# Revit family: Wide Flange-Profile
name_source: partatom
category: Profiles
revit_build: Autodesk Revit Architecture 2012 (Build: 20110210_1515)
units: mm (PartAtom-declared; Revit-internal decimal feet)

## types (267) — shared parameters

## per-type parameters (varying)
| type | A | W | bf | d | k | tf | tw |
| W44X335 | 0.68 SF | 335 | 1' - 3 15/16" | 3' - 8 1/32" | 0' - 2 5/8" | 0' - 1 25/32" | 0' - 1 1/32" |
| W44X290 | 0.6 SF | 290 | 1' - 3 13/16" | 3' - 7 5/8" | 0' - 2 7/16" | 0' - 1 9/16" | 0' - 0 7/8" |
| W44X262 | 0.54 SF | 262 | 1' - 3 3/4" | 3' - 7 5/16" | 0' - 2 1/4" | 0' - 1 13/32" | 0' - 0 25/32" |
| W44X230 | 0.47 SF | 230 | 1' - 3 3/4" | 3' - 6 29/32" | 0' - 2 1/16" | 0' - 1 7/32" | 0' - 0 23/32" |
| W40X593 | 1.21 SF | 593 | 1' - 4 11/16" | 3' - 7" | 0' - 4 1/2" | 0' - 3 7/32" | 0' - 1 25/32" |
| W40X503 | 1.03 SF | 503 | 1' - 4 13/32" | 3' - 6 1/16" | 0' - 4" | 0' - 2 3/4" | 0' - 1 17/32" |
| W40X431 | 0.88 SF | 431 | 1' - 4 7/32" | 3' - 5 1/4" | 0' - 3 5/8" | 0' - 2 3/8" | 0' - 1 11/32" |
| W40X397 | 0.81 SF | 397 | 1' - 4 1/8" | 3' - 4 15/16" | 0' - 3 1/2" | 0' - 2 3/16" | 0' - 1 7/32" |
| W40X372 | 0.76 SF | 372 | 1' - 4 1/16" | 3' - 4 5/8" | 0' - 3 5/16" | 0' - 2 1/32" | 0' - 1 5/32" |
| W40X362 | 0.74 SF | 362 | 1' - 4 1/32" | 3' - 4 9/16" | 0' - 3 1/4" | 0' - 2" | 0' - 1 1/8" |
| W40X324 | 0.66 SF | 324 | 1' - 3 29/32" | 3' - 4 5/32" | 0' - 3 1/16" | 0' - 1 13/16" | 0' - 1" |
| W40X297 | 0.61 SF | 297 | 1' - 3 13/16" | 3' - 3 27/32" | 0' - 2 15/16" | 0' - 1 21/32" | 0' - 0 15/16" |
| W40X277 | 0.57 SF | 277 | 1' - 3 27/32" | 3' - 3 11/16" | 0' - 2 7/8" | 0' - 1 9/16" | 0' - 0 27/32" |
| W40X249 | 0.51 SF | 249 | 1' - 3 3/4" | 3' - 3 3/8" | 0' - 2 11/16" | 0' - 1 13/32" | 0' - 0 3/4" |
| W40X215 | 0.44 SF | 215 | 1' - 3 3/4" | 3' - 2 31/32" | 0' - 2 1/2" | 0' - 1 7/32" | 0' - 0 21/32" |
| W40X199 | 0.41 SF | 199 | 1' - 3 3/4" | 3' - 2 21/32" | 0' - 2 5/16" | 0' - 1 1/16" | 0' - 0 21/32" |
| W40X392 | 0.8 SF | 392 | 1' - 0 3/8" | 3' - 5 9/16" | 0' - 3 13/16" | 0' - 2 17/32" | 0' - 1 13/32" |
| W40X331 | 0.68 SF | 331 | 1' - 0 5/32" | 3' - 4 5/32" | 0' - 3 3/8" | 0' - 2 1/8" | 0' - 1 7/32" |
| W40X327 | 0.67 SF | 327 | 1' - 0 1/8" | 3' - 4 13/16" | 0' - 3 3/8" | 0' - 2 1/8" | 0' - 1 3/16" |
| W40X278 | 0.57 SF | 278 | 1' - 0" | 3' - 4 5/32" | 0' - 3 1/16" | 0' - 1 13/16" | 0' - 1 1/32" |
| W40X264 | 0.54 SF | 264 | 0' - 11 31/32" | 3' - 4" | 0' - 3" | 0' - 1 23/32" | 0' - 0 31/32" |
| W40X235 | 0.48 SF | 235 | 0' - 11 15/16" | 3' - 3 11/16" | 0' - 2 7/8" | 0' - 1 9/16" | 0' - 0 27/32" |
| W40X211 | 0.43 SF | 211 | 0' - 11 7/8" | 3' - 3 3/8" | 0' - 2 11/16" | 0' - 1 13/32" | 0' - 0 3/4" |
| W40X183 | 0.37 SF | 183 | 0' - 11 13/16" | 3' - 2 31/32" | 0' - 2 1/2" | 0' - 1 3/16" | 0' - 0 21/32" |
| W40X167 | 0.34 SF | 167 | 0' - 11 13/16" | 3' - 2 19/32" | 0' - 2 5/16" | 0' - 1 1/32" | 0' - 0 21/32" |
| W40X149 | 0.3 SF | 149 | 0' - 11 13/16" | 3' - 2 3/16" | 0' - 2 1/8" | 0' - 0 27/32" | 0' - 0 5/8" |
| W36X798 | 1.63 SF | 798 | 1' - 6" | 3' - 5 31/32" | 0' - 5 9/16" | 0' - 4 9/32" | 0' - 2 3/8" |
| W36X650 | 1.33 SF | 650 | 1' - 5 9/16" | 3' - 4 15/32" | 0' - 4 13/16" | 0' - 3 17/32" | 0' - 1 31/32" |
| W36X527 | 1.08 SF | 527 | 1' - 5 7/32" | 3' - 3 7/32" | 0' - 4 3/16" | 0' - 2 29/32" | 0' - 1 5/8" |
| W36X439 | 0.9 SF | 439 | 1' - 4 31/32" | 3' - 2 1/4" | 0' - 3 11/16" | 0' - 2 7/16" | 0' - 1 3/8" |
| W36X393 | 0.81 SF | 393 | 1' - 4 27/32" | 3' - 1 13/16" | 0' - 3 7/16" | 0' - 2 3/16" | 0' - 1 7/32" |
| W36X359 | 0.73 SF | 359 | 1' - 4 23/32" | 3' - 1 13/32" | 0' - 3 1/4" | 0' - 2" | 0' - 1 1/8" |
| W36X328 | 0.67 SF | 328 | 1' - 4 5/8" | 3' - 1 3/32" | 0' - 3 1/8" | 0' - 1 27/32" | 0' - 1 1/32" |
| W36X300 | 0.61 SF | 300 | 1' - 4 21/32" | 3' - 0 3/4" | 0' - 2 15/16" | 0' - 1 11/16" | 0' - 0 15/16" |
| W36X280 | 0.57 SF | 280 | 1' - 4 19/32" | 3' - 0 17/32" | 0' - 2 13/16" | 0' - 1 9/16" | 0' - 0 7/8" |
| W36X260 | 0.53 SF | 260 | 1' - 4 9/16" | 3' - 0 1/4" | 0' - 2 11/16" | 0' - 1 7/16" | 0' - 0 27/32" |
| W36X245 | 0.5 SF | 245 | 1' - 4 1/2" | 3' - 0 3/32" | 0' - 2 5/8" | 0' - 1 11/32" | 0' - 0 13/16" |
| W36X230 | 0.47 SF | 230 | 1' - 4 15/32" | 2' - 11 29/32" | 0' - 2 1/2" | 0' - 1 1/4" | 0' - 0 3/4" |
| W36X256 | 0.52 SF | 256 | 1' - 0 7/32" | 3' - 1 7/16" | 0' - 2 5/8" | 0' - 1 23/32" | 0' - 0 31/32" |
| W36X232 | 0.47 SF | 232 | 1' - 0 1/8" | 3' - 1 1/8" | 0' - 2 7/16" | 0' - 1 9/16" | 0' - 0 7/8" |
| W36X210 | 0.43 SF | 210 | 1' - 0 3/16" | 3' - 0 11/16" | 0' - 2 5/16" | 0' - 1 3/8" | 0' - 0 27/32" |
| W36X194 | 0.4 SF | 194 | 1' - 0 1/8" | 3' - 0 1/2" | 0' - 2 3/16" | 0' - 1 1/4" | 0' - 0 3/4" |
| W36X182 | 0.37 SF | 182 | 1' - 0 1/16" | 3' - 0 11/32" | 0' - 2 1/8" | 0' - 1 3/16" | 0' - 0 23/32" |
| W36X170 | 0.35 SF | 170 | 1' - 0 1/32" | 3' - 0 5/32" | 0' - 2" | 0' - 1 3/32" | 0' - 0 11/16" |
| W36X160 | 0.33 SF | 160 | 1' - 0" | 3' - 0" | 0' - 1 15/16" | 0' - 1 1/32" | 0' - 0 21/32" |
| W36X150 | 0.31 SF | 150 | 0' - 11 31/32" | 2' - 11 27/32" | 0' - 1 7/8" | 0' - 0 15/16" | 0' - 0 5/8" |
| W36X135 | 0.28 SF | 135 | 0' - 11 15/16" | 2' - 11 9/16" | 0' - 1 11/16" | 0' - 0 25/32" | 0' - 0 19/32" |
| W33X387 | 0.79 SF | 387 | 1' - 4 3/16" | 2' - 11 9/16" | 0' - 3 3/16" | 0' - 2 9/32" | 0' - 1 1/4" |
| W33X354 | 0.72 SF | 354 | 1' - 4 3/32" | 2' - 11 9/16" | 0' - 2 15/16" | 0' - 2 3/32" | 0' - 1 5/32" |
| W33X318 | 0.65 SF | 318 | 1' - 4" | 2' - 11 5/32" | 0' - 2 3/4" | 0' - 1 7/8" | 0' - 1 1/32" |
| W33X291 | 0.6 SF | 291 | 1' - 3 29/32" | 2' - 10 27/32" | 0' - 2 5/8" | 0' - 1 23/32" | 0' - 0 31/32" |
| W33X263 | 0.54 SF | 263 | 1' - 3 13/16" | 2' - 10 17/32" | 0' - 2 7/16" | 0' - 1 9/16" | 0' - 0 7/8" |
| W33X241 | 0.49 SF | 241 | 1' - 3 7/8" | 2' - 10 3/16" | 0' - 2 1/4" | 0' - 1 13/32" | 0' - 0 27/32" |
| W33X221 | 0.45 SF | 221 | 1' - 3 13/16" | 2' - 9 15/16" | 0' - 2 1/8" | 0' - 1 9/32" | 0' - 0 25/32" |
| W33X201 | 0.41 SF | 201 | 1' - 3 3/4" | 2' - 9 11/16" | 0' - 2" | 0' - 1 5/32" | 0' - 0 23/32" |
| W33X169 | 0.34 SF | 169 | 0' - 11 1/2" | 2' - 9 13/16" | 0' - 2 1/8" | 0' - 1 7/32" | 0' - 0 21/32" |
| W33X152 | 0.31 SF | 152 | 0' - 11 9/16" | 2' - 9 1/2" | 0' - 1 15/16" | 0' - 1 1/16" | 0' - 0 5/8" |
| W33X141 | 0.29 SF | 141 | 0' - 11 17/32" | 2' - 9 5/16" | 0' - 1 13/16" | 0' - 0 31/32" | 0' - 0 19/32" |
| W33X130 | 0.27 SF | 130 | 0' - 11 1/2" | 2' - 9 3/32" | 0' - 1 3/4" | 0' - 0 27/32" | 0' - 0 19/32" |
| W33X118 | 0.24 SF | 118 | 0' - 11 15/32" | 2' - 8 7/8" | 0' - 1 5/8" | 0' - 0 3/4" | 0' - 0 9/16" |
| W30X391 | 0.8 SF | 391 | 1' - 3 19/32" | 2' - 9 3/16" | 0' - 3 3/8" | 0' - 2 7/16" | 0' - 1 3/8" |
| W30X357 | 0.73 SF | 357 | 1' - 3 15/32" | 2' - 8 13/16" | 0' - 3 1/8" | 0' - 2 1/4" | 0' - 1 1/4" |
| W30X326 | 0.67 SF | 326 | 1' - 3 3/8" | 2' - 8 13/32" | 0' - 2 15/16" | 0' - 2 1/16" | 0' - 1 1/8" |
| W30X292 | 0.6 SF | 292 | 1' - 3 1/4" | 2' - 8" | 0' - 2 3/4" | 0' - 1 27/32" | 0' - 1 1/32" |
| W30X261 | 0.53 SF | 261 | 1' - 3 5/32" | 2' - 7 5/8" | 0' - 2 9/16" | 0' - 1 21/32" | 0' - 0 15/16" |
| W30X235 | 0.48 SF | 235 | 1' - 3 1/16" | 2' - 7 5/16" | 0' - 2 3/8" | 0' - 1 1/2" | 0' - 0 27/32" |
| W30X211 | 0.43 SF | 211 | 1' - 3 3/32" | 2' - 6 15/16" | 0' - 2 1/4" | 0' - 1 5/16" | 0' - 0 25/32" |
| W30X191 | 0.39 SF | 191 | 1' - 3 1/32" | 2' - 6 11/16" | 0' - 2 1/16" | 0' - 1 3/16" | 0' - 0 23/32" |
| W30X173 | 0.35 SF | 173 | 1' - 3" | 2' - 6 7/16" | 0' - 2" | 0' - 1 1/16" | 0' - 0 21/32" |
| W30X148 | 0.3 SF | 148 | 0' - 10 15/32" | 2' - 6 21/32" | 0' - 2 1/16" | 0' - 1 3/16" | 0' - 0 21/32" |
| W30X132 | 0.27 SF | 132 | 0' - 10 17/32" | 2' - 6 5/16" | 0' - 1 7/8" | 0' - 1" | 0' - 0 5/8" |
| W30X124 | 0.25 SF | 124 | 0' - 10 1/2" | 2' - 6 5/32" | 0' - 1 13/16" | 0' - 0 15/16" | 0' - 0 19/32" |
| W30X116 | 0.24 SF | 116 | 0' - 10 1/2" | 2' - 6" | 0' - 1 3/4" | 0' - 0 27/32" | 0' - 0 9/16" |
| W30X108 | 0.22 SF | 108 | 0' - 10 15/32" | 2' - 5 27/32" | 0' - 1 11/16" | 0' - 0 3/4" | 0' - 0 17/32" |
| W30X99 | 0.2 SF | 99 | 0' - 10 7/16" | 2' - 5 21/32" | 0' - 1 9/16" | 0' - 0 21/32" | 0' - 0 17/32" |
| W30X90 | 0.18 SF | 90 | 0' - 10 13/32" | 2' - 5 17/32" | 0' - 1 1/2" | 0' - 0 5/8" | 0' - 0 15/32" |
| W27X539 | 1.1 SF | 539 | 1' - 3 1/4" | 2' - 8 17/32" | 0' - 4 7/16" | 0' - 3 17/32" | 0' - 1 31/32" |
| W27X368 | 0.75 SF | 368 | 1' - 2 21/32" | 2' - 7 13/32" | 0' - 3 3/8" | 0' - 2 15/32" | 0' - 1 3/8" |
| W27X336 | 0.69 SF | 336 | 1' - 2 9/16" | 2' - 6" | 0' - 3 3/16" | 0' - 2 9/32" | 0' - 1 1/4" |
| W27X307 | 0.63 SF | 307 | 1' - 2 7/16" | 2' - 5 5/8" | 0' - 3" | 0' - 2 3/32" | 0' - 1 5/32" |
| W27X281 | 0.58 SF | 281 | 1' - 2 11/32" | 2' - 5 9/32" | 0' - 2 13/16" | 0' - 1 15/16" | 0' - 1 1/16" |
| W27X258 | 0.53 SF | 258 | 1' - 2 9/32" | 2' - 4 31/32" | 0' - 2 11/16" | 0' - 1 25/32" | 0' - 0 31/32" |
| W27X235 | 0.48 SF | 235 | 1' - 2 3/16" | 2' - 4 21/32" | 0' - 2 1/2" | 0' - 1 5/8" | 0' - 0 29/32" |
| W27X217 | 0.44 SF | 217 | 1' - 2 1/8" | 2' - 4 7/16" | 0' - 2 3/8" | 0' - 1 1/2" | 0' - 0 27/32" |
| W27X194 | 0.4 SF | 194 | 1' - 2 1/32" | 2' - 4 1/8" | 0' - 2 1/4" | 0' - 1 11/32" | 0' - 0 3/4" |
| W27X178 | 0.36 SF | 178 | 1' - 2 3/32" | 2' - 3 13/16" | 0' - 2 1/16" | 0' - 1 3/16" | 0' - 0 23/32" |
| W27X161 | 0.33 SF | 161 | 1' - 2 1/32" | 2' - 3 19/32" | 0' - 2" | 0' - 1 3/32" | 0' - 0 21/32" |
| W27X146 | 0.3 SF | 146 | 1' - 1 31/32" | 2' - 3 3/8" | 0' - 1 7/8" | 0' - 0 31/32" | 0' - 0 19/32" |
| W27X129 | 0.26 SF | 129 | 0' - 10" | 2' - 3 5/8" | 0' - 2" | 0' - 1 3/32" | 0' - 0 5/8" |
| W27X114 | 0.23 SF | 114 | 0' - 10 1/16" | 2' - 3 9/32" | 0' - 1 13/16" | 0' - 0 15/16" | 0' - 0 9/16" |
| W27X102 | 0.21 SF | 102 | 0' - 10" | 2' - 3 3/32" | 0' - 1 3/4" | 0' - 0 27/32" | 0' - 0 1/2" |
| W27X94 | 0.19 SF | 94 | 0' - 10" | 2' - 2 29/32" | 0' - 1 5/8" | 0' - 0 3/4" | 0' - 0 1/2" |
| W27X84 | 0.17 SF | 84 | 0' - 9 31/32" | 2' - 2 23/32" | 0' - 1 9/16" | 0' - 0 5/8" | 0' - 0 15/32" |
| W24X370 | 0.76 SF | 370 | 1' - 1 21/32" | 2' - 4" | 0' - 3 5/8" | 0' - 2 23/32" | 0' - 1 17/32" |
| W24X335 | 0.68 SF | 335 | 1' - 1 17/32" | 2' - 3 17/32" | 0' - 3 3/8" | 0' - 2 15/32" | 0' - 1 3/8" |
| W24X306 | 0.62 SF | 306 | 1' - 1 13/32" | 2' - 3 1/8" | 0' - 3 3/16" | 0' - 2 9/32" | 0' - 1 1/4" |
| W24X279 | 0.57 SF | 279 | 1' - 1 5/16" | 2' - 2 23/32" | 0' - 3" | 0' - 2 3/32" | 0' - 1 5/32" |
| W24X250 | 0.51 SF | 250 | 1' - 1 3/16" | 2' - 2 11/32" | 0' - 2 13/16" | 0' - 1 7/8" | 0' - 1 1/32" |
| W24X229 | 0.47 SF | 229 | 1' - 1 1/8" | 2' - 2 1/32" | 0' - 2 5/8" | 0' - 1 23/32" | 0' - 0 31/32" |
| W24X207 | 0.42 SF | 207 | 1' - 1" | 2' - 1 23/32" | 0' - 2 1/2" | 0' - 1 9/16" | 0' - 0 7/8" |
| W24X192 | 0.39 SF | 192 | 1' - 0 15/16" | 2' - 1 15/32" | 0' - 2 3/8" | 0' - 1 15/32" | 0' - 0 13/16" |
| W24X176 | 0.36 SF | 176 | 1' - 0 7/8" | 2' - 1 1/4" | 0' - 2 1/4" | 0' - 1 11/32" | 0' - 0 3/4" |
| W24X162 | 0.33 SF | 162 | 1' - 0 31/32" | 2' - 1" | 0' - 2 1/8" | 0' - 1 7/32" | 0' - 0 23/32" |
| W24X146 | 0.3 SF | 146 | 1' - 0 29/32" | 2' - 0 3/4" | 0' - 2" | 0' - 1 3/32" | 0' - 0 21/32" |
| W24X131 | 0.27 SF | 131 | 1' - 0 27/32" | 2' - 0 15/32" | 0' - 1 7/8" | 0' - 0 31/32" | 0' - 0 19/32" |
| W24X117 | 0.24 SF | 117 | 1' - 0 13/16" | 2' - 0 1/4" | 0' - 1 3/4" | 0' - 0 27/32" | 0' - 0 9/16" |
| W24X104 | 0.21 SF | 104 | 1' - 0 3/4" | 2' - 0 1/16" | 0' - 1 5/8" | 0' - 0 3/4" | 0' - 0 1/2" |
| W24X103 | 0.21 SF | 103 | 0' - 9" | 2' - 0 17/32" | 0' - 1 7/8" | 0' - 0 31/32" | 0' - 0 9/16" |
| W24X94 | 0.19 SF | 94 | 0' - 9 1/16" | 2' - 0 5/16" | 0' - 1 3/4" | 0' - 0 7/8" | 0' - 0 1/2" |
| W24X84 | 0.17 SF | 84 | 0' - 9 1/32" | 2' - 0 3/32" | 0' - 1 11/16" | 0' - 0 25/32" | 0' - 0 15/32" |
| W24X76 | 0.16 SF | 76 | 0' - 9" | 1' - 11 29/32" | 0' - 1 9/16" | 0' - 0 11/16" | 0' - 0 7/16" |
| W24X68 | 0.14 SF | 68 | 0' - 8 31/32" | 1' - 11 23/32" | 0' - 1 1/2" | 0' - 0 19/32" | 0' - 0 13/32" |
| W24X62 | 0.13 SF | 62 | 0' - 7 1/32" | 1' - 11 3/4" | 0' - 1 1/2" | 0' - 0 19/32" | 0' - 0 7/16" |
| W24X55 | 0.11 SF | 55 | 0' - 7" | 1' - 11 9/16" | 0' - 1 7/16" | 0' - 0 1/2" | 0' - 0 13/32" |
| W21X201 | 0.41 SF | 201 | 1' - 0 9/16" | 1' - 11 1/32" | 0' - 2 1/2" | 0' - 1 5/8" | 0' - 0 29/32" |
| W21X182 | 0.37 SF | 182 | 1' - 0 1/2" | 1' - 10 23/32" | 0' - 2 3/8" | 0' - 1 15/32" | 0' - 0 27/32" |
| W21X166 | 0.34 SF | 166 | 1' - 0 13/32" | 1' - 10 15/32" | 0' - 2 1/4" | 0' - 1 3/8" | 0' - 0 3/4" |
| W21X147 | 0.3 SF | 147 | 1' - 0 1/2" | 1' - 10 1/16" | 0' - 2" | 0' - 1 5/32" | 0' - 0 23/32" |
| W21X132 | 0.27 SF | 132 | 1' - 0 7/16" | 1' - 9 27/32" | 0' - 1 15/16" | 0' - 1 1/32" | 0' - 0 21/32" |
| W21X122 | 0.25 SF | 122 | 1' - 0 3/8" | 1' - 9 11/16" | 0' - 1 13/16" | 0' - 0 31/32" | 0' - 0 19/32" |
| W21X111 | 0.23 SF | 111 | 1' - 0 11/32" | 1' - 9 1/2" | 0' - 1 3/4" | 0' - 0 7/8" | 0' - 0 9/16" |
| W21X101 | 0.21 SF | 101 | 1' - 0 9/32" | 1' - 9 3/8" | 0' - 1 11/16" | 0' - 0 13/16" | 0' - 0 1/2" |
| W21X93 | 0.19 SF | 93 | 0' - 8 13/32" | 1' - 9 5/8" | 0' - 1 5/8" | 0' - 0 15/16" | 0' - 0 19/32" |
| W21X83 | 0.17 SF | 83 | 0' - 8 11/32" | 1' - 9 7/16" | 0' - 1 1/2" | 0' - 0 27/32" | 0' - 0 1/2" |
| W21X73 | 0.15 SF | 73 | 0' - 8 9/32" | 1' - 9 1/4" | 0' - 1 7/16" | 0' - 0 3/4" | 0' - 0 15/32" |
| W21X68 | 0.14 SF | 68 | 0' - 8 9/32" | 1' - 9 1/8" | 0' - 1 3/8" | 0' - 0 11/16" | 0' - 0 7/16" |
| W21X62 | 0.13 SF | 62 | 0' - 8 1/4" | 1' - 9" | 0' - 1 5/16" | 0' - 0 5/8" | 0' - 0 13/32" |
| W21X55 | 0.11 SF | 55 | 0' - 8 7/32" | 1' - 8 13/16" | 0' - 1 3/16" | 0' - 0 17/32" | 0' - 0 3/8" |
| W21X48 | 0.1 SF | 48 | 0' - 8 1/8" | 1' - 8 19/32" | 0' - 1 1/8" | 0' - 0 7/16" | 0' - 0 11/32" |
| W21X57 | 0.12 SF | 57 | 0' - 6 9/16" | 1' - 9 1/16" | 0' - 1 5/16" | 0' - 0 21/32" | 0' - 0 13/32" |
| W21X50 | 0.1 SF | 50 | 0' - 6 17/32" | 1' - 8 27/32" | 0' - 1 1/4" | 0' - 0 17/32" | 0' - 0 3/8" |
| W21X44 | 0.09 SF | 44 | 0' - 6 1/2" | 1' - 8 21/32" | 0' - 1 1/8" | 0' - 0 7/16" | 0' - 0 11/32" |
| W18X175 | 0.36 SF | 175 | 0' - 11 3/8" | 1' - 8 1/32" | 0' - 2 7/16" | 0' - 1 19/32" | 0' - 0 7/8" |
| W18X158 | 0.32 SF | 158 | 0' - 11 5/16" | 1' - 7 23/32" | 0' - 2 3/8" | 0' - 1 7/16" | 0' - 0 13/16" |
| W18X143 | 0.29 SF | 143 | 0' - 11 7/32" | 1' - 7 1/2" | 0' - 2 3/16" | 0' - 1 5/16" | 0' - 0 23/32" |
| W18X130 | 0.27 SF | 130 | 0' - 11 5/32" | 1' - 7 1/4" | 0' - 2 1/16" | 0' - 1 3/16" | 0' - 0 21/32" |
| W18X119 | 0.24 SF | 119 | 0' - 11 1/4" | 1' - 6 31/32" | 0' - 1 15/16" | 0' - 1 1/16" | 0' - 0 21/32" |
| W18X106 | 0.22 SF | 106 | 0' - 11 3/16" | 1' - 6 23/32" | 0' - 1 13/16" | 0' - 0 15/16" | 0' - 0 19/32" |
| W18X97 | 0.2 SF | 97 | 0' - 11 5/32" | 1' - 6 19/32" | 0' - 1 3/4" | 0' - 0 7/8" | 0' - 0 17/32" |
| W18X86 | 0.18 SF | 86 | 0' - 11 3/32" | 1' - 6 3/8" | 0' - 1 5/8" | 0' - 0 25/32" | 0' - 0 15/32" |
| W18X76 | 0.15 SF | 76 | 0' - 11 1/32" | 1' - 6 7/32" | 0' - 1 9/16" | 0' - 0 11/16" | 0' - 0 7/16" |
| W18X71 | 0.14 SF | 71 | 0' - 7 5/8" | 1' - 6 15/32" | 0' - 1 1/2" | 0' - 0 13/16" | 0' - 0 1/2" |
| W18X65 | 0.13 SF | 65 | 0' - 7 19/32" | 1' - 6 11/32" | 0' - 1 7/16" | 0' - 0 3/4" | 0' - 0 7/16" |
| W18X60 | 0.12 SF | 60 | 0' - 7 9/16" | 1' - 6 1/4" | 0' - 1 3/8" | 0' - 0 11/16" | 0' - 0 13/32" |
| W18X55 | 0.11 SF | 55 | 0' - 7 17/32" | 1' - 6 1/8" | 0' - 1 5/16" | 0' - 0 5/8" | 0' - 0 3/8" |
| W18X50 | 0.1 SF | 50 | 0' - 7 1/2" | 1' - 6" | 0' - 1 1/4" | 0' - 0 9/16" | 0' - 0 11/32" |
| W18X46 | 0.09 SF | 46 | 0' - 6 1/16" | 1' - 6 1/16" | 0' - 1 1/4" | 0' - 0 19/32" | 0' - 0 3/8" |
| W18X40 | 0.08 SF | 40 | 0' - 6" | 1' - 5 29/32" | 0' - 1 3/16" | 0' - 0 17/32" | 0' - 0 5/16" |
| W18X35 | 0.07 SF | 35 | 0' - 6" | 1' - 5 11/16" | 0' - 1 1/8" | 0' - 0 7/16" | 0' - 0 5/16" |
| W16X100 | 0.21 SF | 100 | 0' - 10 7/16" | 1' - 4 31/32" | 0' - 1 7/8" | 0' - 1" | 0' - 0 19/32" |
| W16X89 | 0.18 SF | 89 | 0' - 10 3/8" | 1' - 4 3/4" | 0' - 1 3/4" | 0' - 0 7/8" | 0' - 0 17/32" |
| W16X77 | 0.16 SF | 77 | 0' - 10 9/32" | 1' - 4 17/32" | 0' - 1 5/8" | 0' - 0 3/4" | 0' - 0 15/32" |
| W16X67 | 0.14 SF | 67 | 0' - 10 1/4" | 1' - 4 11/32" | 0' - 1 9/16" | 0' - 0 21/32" | 0' - 0 13/32" |
| W16X57 | 0.12 SF | 57 | 0' - 7 1/8" | 1' - 4 7/16" | 0' - 1 3/8" | 0' - 0 23/32" | 0' - 0 7/16" |
| W16X50 | 0.1 SF | 50 | 0' - 7 1/16" | 1' - 4 1/4" | 0' - 1 5/16" | 0' - 0 5/8" | 0' - 0 3/8" |
| W16X45 | 0.09 SF | 45 | 0' - 7 1/32" | 1' - 4 1/8" | 0' - 1 1/4" | 0' - 0 9/16" | 0' - 0 11/32" |
| W16X40 | 0.08 SF | 40 | 0' - 7" | 1' - 4" | 0' - 1 3/16" | 0' - 0 1/2" | 0' - 0 5/16" |
| W16X36 | 0.07 SF | 36 | 0' - 7" | 1' - 3 7/8" | 0' - 1 1/8" | 0' - 0 7/16" | 0' - 0 9/32" |
| W16X31 | 0.06 SF | 31 | 0' - 5 17/32" | 1' - 3 7/8" | 0' - 1 1/8" | 0' - 0 7/16" | 0' - 0 9/32" |
| W16X26 | 0.05 SF | 26 | 0' - 5 1/2" | 1' - 3 11/16" | 0' - 1 1/16" | 0' - 0 11/32" | 0' - 0 1/4" |
| W14X808 | 1.65 SF | 808 | 1' - 6 9/16" | 1' - 10 27/32" | 0' - 6 7/16" | 0' - 5 1/8" | 0' - 3 3/4" |
| W14X730 | 1.49 SF | 730 | 1' - 5 7/8" | 1' - 10 13/32" | 0' - 6 3/16" | 0' - 4 29/32" | 0' - 3 1/16" |
| W14X665 | 1.36 SF | 665 | 1' - 5 21/32" | 1' - 9 5/8" | 0' - 5 13/16" | 0' - 4 17/32" | 0' - 2 27/32" |
| W14X605 | 1.24 SF | 605 | 1' - 5 13/32" | 1' - 8 29/32" | 0' - 5 7/16" | 0' - 4 5/32" | 0' - 2 19/32" |
| W14X550 | 1.13 SF | 550 | 1' - 5 3/16" | 1' - 8 1/4" | 0' - 5 1/8" | 0' - 3 13/16" | 0' - 2 3/8" |
| W14X500 | 1.02 SF | 500 | 1' - 5" | 1' - 7 19/32" | 0' - 4 13/16" | 0' - 3 1/2" | 0' - 2 3/16" |
| W14X455 | 0.93 SF | 455 | 1' - 4 27/32" | 1' - 7 1/32" | 0' - 4 1/2" | 0' - 3 7/32" | 0' - 2" |
| W14X426 | 0.87 SF | 426 | 1' - 4 11/16" | 1' - 6 21/32" | 0' - 4 5/16" | 0' - 3 1/32" | 0' - 1 7/8" |
| W14X398 | 0.81 SF | 398 | 1' - 4 19/32" | 1' - 6 9/32" | 0' - 4 1/8" | 0' - 2 27/32" | 0' - 1 25/32" |
| W14X370 | 0.76 SF | 370 | 1' - 4 15/32" | 1' - 5 29/32" | 0' - 3 15/16" | 0' - 2 21/32" | 0' - 1 21/32" |
| W14X342 | 0.7 SF | 342 | 1' - 4 3/8" | 1' - 5 17/32" | 0' - 3 3/4" | 0' - 2 15/32" | 0' - 1 17/32" |
| W14X311 | 0.63 SF | 311 | 1' - 4 7/32" | 1' - 5 1/8" | 0' - 3 9/16" | 0' - 2 1/4" | 0' - 1 13/32" |
| W14X283 | 0.58 SF | 283 | 1' - 4 1/8" | 1' - 4 3/4" | 0' - 3 3/8" | 0' - 2 1/16" | 0' - 1 9/32" |
| W14X257 | 0.53 SF | 257 | 1' - 4" | 1' - 4 3/8" | 0' - 3 3/16" | 0' - 1 7/8" | 0' - 1 3/16" |
| W14X233 | 0.48 SF | 233 | 1' - 3 7/8" | 1' - 4 1/32" | 0' - 3" | 0' - 1 23/32" | 0' - 1 1/16" |
| W14X211 | 0.43 SF | 211 | 1' - 3 13/16" | 1' - 3 23/32" | 0' - 2 7/8" | 0' - 1 9/16" | 0' - 0 31/32" |
| W14X193 | 0.39 SF | 193 | 1' - 3 23/32" | 1' - 3 15/32" | 0' - 2 3/4" | 0' - 1 7/16" | 0' - 0 7/8" |
| W14X176 | 0.36 SF | 176 | 1' - 3 21/32" | 1' - 3 7/32" | 0' - 2 5/8" | 0' - 1 5/16" | 0' - 0 27/32" |
| W14X159 | 0.32 SF | 159 | 1' - 3 9/16" | 1' - 2 31/32" | 0' - 2 1/2" | 0' - 1 3/16" | 0' - 0 3/4" |
| W14X145 | 0.3 SF | 145 | 1' - 3 1/2" | 1' - 2 25/32" | 0' - 2 3/8" | 0' - 1 3/32" | 0' - 0 11/16" |
| W14X132 | 0.27 SF | 132 | 1' - 2 23/32" | 1' - 2 21/32" | 0' - 2 5/16" | 0' - 1 1/32" | 0' - 0 21/32" |
| W14X120 | 0.25 SF | 120 | 1' - 2 21/32" | 1' - 2 15/32" | 0' - 2 1/4" | 0' - 0 15/16" | 0' - 0 19/32" |
| W14X109 | 0.22 SF | 109 | 1' - 2 19/32" | 1' - 2 5/16" | 0' - 2 3/16" | 0' - 0 7/8" | 0' - 0 17/32" |
| W14X99 | 0.2 SF | 99 | 1' - 2 9/16" | 1' - 2 5/32" | 0' - 2 1/16" | 0' - 0 25/32" | 0' - 0 1/2" |
| W14X90 | 0.18 SF | 90 | 1' - 2 17/32" | 1' - 2 1/32" | 0' - 2" | 0' - 0 23/32" | 0' - 0 7/16" |
| W14X82 | 0.17 SF | 82 | 0' - 10 1/8" | 1' - 2 5/16" | 0' - 1 11/16" | 0' - 0 27/32" | 0' - 0 1/2" |
| W14X74 | 0.15 SF | 74 | 0' - 10 1/16" | 1' - 2 5/32" | 0' - 1 5/8" | 0' - 0 25/32" | 0' - 0 7/16" |
| W14X68 | 0.14 SF | 68 | 0' - 10 1/32" | 1' - 2 1/32" | 0' - 1 9/16" | 0' - 0 23/32" | 0' - 0 13/32" |
| W14X61 | 0.12 SF | 61 | 0' - 10" | 1' - 1 7/8" | 0' - 1 1/2" | 0' - 0 21/32" | 0' - 0 3/8" |
| W14X53 | 0.11 SF | 53 | 0' - 8 1/16" | 1' - 1 29/32" | 0' - 1 1/2" | 0' - 0 21/32" | 0' - 0 3/8" |
| W14X48 | 0.1 SF | 48 | 0' - 8 1/32" | 1' - 1 25/32" | 0' - 1 7/16" | 0' - 0 19/32" | 0' - 0 11/32" |
| W14X43 | 0.09 SF | 43 | 0' - 8" | 1' - 1 21/32" | 0' - 1 3/8" | 0' - 0 17/32" | 0' - 0 5/16" |
| W14X38 | 0.08 SF | 38 | 0' - 6 25/32" | 1' - 2 3/32" | 0' - 1 1/4" | 0' - 0 1/2" | 0' - 0 5/16" |
| W14X34 | 0.07 SF | 34 | 0' - 6 3/4" | 1' - 1 31/32" | 0' - 1 3/16" | 0' - 0 15/32" | 0' - 0 9/32" |
| W14X30 | 0.06 SF | 30 | 0' - 6 23/32" | 1' - 1 27/32" | 0' - 1 1/8" | 0' - 0 3/8" | 0' - 0 9/32" |
| W14X26 | 0.05 SF | 26 | 0' - 5 1/32" | 1' - 1 29/32" | 0' - 1 1/8" | 0' - 0 13/32" | 0' - 0 1/4" |
| W14X22 | 0.05 SF | 22 | 0' - 5" | 1' - 1 3/4" | 0' - 1 1/16" | 0' - 0 11/32" | 0' - 0 7/32" |
| W12X336 | 0.69 SF | 336 | 1' - 1 3/8" | 1' - 4 13/16" | 0' - 3 7/8" | 0' - 2 31/32" | 0' - 1 25/32" |
| W12X305 | 0.62 SF | 305 | 1' - 1 1/4" | 1' - 4 5/16" | 0' - 3 5/8" | 0' - 2 23/32" | 0' - 1 5/8" |
| W12X279 | 0.57 SF | 279 | 1' - 1 1/8" | 1' - 3 27/32" | 0' - 3 3/8" | 0' - 2 15/32" | 0' - 1 17/32" |
| W12X252 | 0.51 SF | 252 | 1' - 1" | 1' - 3 13/32" | 0' - 3 1/8" | 0' - 2 1/4" | 0' - 1 13/32" |
| W12X230 | 0.47 SF | 230 | 1' - 0 29/32" | 1' - 3 1/16" | 0' - 2 15/16" | 0' - 2 1/16" | 0' - 1 9/32" |
| W12X210 | 0.43 SF | 210 | 1' - 0 25/32" | 1' - 2 23/32" | 0' - 2 13/16" | 0' - 1 29/32" | 0' - 1 3/16" |
| W12X190 | 0.39 SF | 190 | 1' - 0 21/32" | 1' - 2 3/8" | 0' - 2 5/8" | 0' - 1 3/4" | 0' - 1 1/16" |
| W12X170 | 0.35 SF | 170 | 1' - 0 9/16" | 1' - 2 1/32" | 0' - 2 7/16" | 0' - 1 9/16" | 0' - 0 31/32" |
| W12X152 | 0.31 SF | 152 | 1' - 0 15/32" | 1' - 1 23/32" | 0' - 2 5/16" | 0' - 1 13/32" | 0' - 0 7/8" |
| W12X136 | 0.28 SF | 136 | 1' - 0 13/32" | 1' - 1 13/32" | 0' - 2 1/8" | 0' - 1 1/4" | 0' - 0 25/32" |
| W12X120 | 0.25 SF | 120 | 1' - 0 5/16" | 1' - 1 1/8" | 0' - 2" | 0' - 1 3/32" | 0' - 0 23/32" |
| W12X106 | 0.22 SF | 106 | 1' - 0 7/32" | 1' - 0 7/8" | 0' - 1 7/8" | 0' - 1" | 0' - 0 5/8" |
| W12X96 | 0.2 SF | 96 | 1' - 0 5/32" | 1' - 0 23/32" | 0' - 1 13/16" | 0' - 0 29/32" | 0' - 0 9/16" |
| W12X87 | 0.18 SF | 87 | 1' - 0 1/8" | 1' - 0 17/32" | 0' - 1 11/16" | 0' - 0 13/16" | 0' - 0 1/2" |
| W12X79 | 0.16 SF | 79 | 1' - 0 3/32" | 1' - 0 3/8" | 0' - 1 5/8" | 0' - 0 3/4" | 0' - 0 15/32" |
| W12X72 | 0.15 SF | 72 | 1' - 0 1/32" | 1' - 0 1/4" | 0' - 1 9/16" | 0' - 0 21/32" | 0' - 0 7/16" |
| W12X65 | 0.13 SF | 65 | 1' - 0" | 1' - 0 1/8" | 0' - 1 1/2" | 0' - 0 19/32" | 0' - 0 3/8" |
| W12X58 | 0.12 SF | 58 | 0' - 10" | 1' - 0 3/16" | 0' - 1 1/2" | 0' - 0 5/8" | 0' - 0 3/8" |
| W12X53 | 0.11 SF | 53 | 0' - 10" | 1' - 0 1/16" | 0' - 1 3/8" | 0' - 0 9/16" | 0' - 0 11/32" |
| W12X50 | 0.1 SF | 50 | 0' - 8 3/32" | 1' - 0 3/16" | 0' - 1 1/2" | 0' - 0 5/8" | 0' - 0 3/8" |
| W12X45 | 0.09 SF | 45 | 0' - 8 1/32" | 1' - 0 1/16" | 0' - 1 3/8" | 0' - 0 9/16" | 0' - 0 11/32" |
| W12X40 | 0.08 SF | 40 | 0' - 8" | 0' - 11 15/16" | 0' - 1 3/8" | 0' - 0 1/2" | 0' - 0 9/32" |
| W12X35 | 0.07 SF | 35 | 0' - 6 9/16" | 1' - 0 1/2" | 0' - 1 3/16" | 0' - 0 17/32" | 0' - 0 5/16" |
| W12X30 | 0.06 SF | 30 | 0' - 6 17/32" | 1' - 0 11/32" | 0' - 1 1/8" | 0' - 0 7/16" | 0' - 0 1/4" |
| W12X26 | 0.05 SF | 26 | 0' - 6 1/2" | 1' - 0 7/32" | 0' - 1 1/16" | 0' - 0 3/8" | 0' - 0 7/32" |
| W12X22 | 0.05 SF | 22 | 0' - 4 1/32" | 1' - 0 5/16" | 0' - 0 15/16" | 0' - 0 7/16" | 0' - 0 1/4" |
| W12X19 | 0.04 SF | 19 | 0' - 4" | 1' - 0 5/32" | 0' - 0 7/8" | 0' - 0 11/32" | 0' - 0 1/4" |
| W12X16 | 0.03 SF | 16 | 0' - 4" | 1' - 0" | 0' - 0 13/16" | 0' - 0 1/4" | 0' - 0 7/32" |
| W12X14 | 0.03 SF | 14 | 0' - 3 31/32" | 0' - 11 29/32" | 0' - 0 3/4" | 0' - 0 7/32" | 0' - 0 3/16" |
| W10X112 | 0.23 SF | 112 | 0' - 10 13/32" | 0' - 11 3/8" | 0' - 1 15/16" | 0' - 1 1/4" | 0' - 0 3/4" |
| W10X100 | 0.2 SF | 100 | 0' - 10 11/32" | 0' - 11 3/32" | 0' - 1 13/16" | 0' - 1 1/8" | 0' - 0 11/16" |
| W10X88 | 0.18 SF | 88 | 0' - 10 1/4" | 0' - 10 27/32" | 0' - 1 11/16" | 0' - 1" | 0' - 0 19/32" |
| W10X77 | 0.16 SF | 77 | 0' - 10 3/16" | 0' - 10 19/32" | 0' - 1 9/16" | 0' - 0 7/8" | 0' - 0 17/32" |
| W10X68 | 0.14 SF | 68 | 0' - 10 1/8" | 0' - 10 13/32" | 0' - 1 7/16" | 0' - 0 25/32" | 0' - 0 15/32" |
| W10X60 | 0.12 SF | 60 | 0' - 10 3/32" | 0' - 10 7/32" | 0' - 1 3/8" | 0' - 0 11/16" | 0' - 0 13/32" |
| W10X54 | 0.11 SF | 54 | 0' - 10 1/32" | 0' - 10 3/32" | 0' - 1 5/16" | 0' - 0 5/8" | 0' - 0 3/8" |
| W10X49 | 0.1 SF | 49 | 0' - 10" | 0' - 9 31/32" | 0' - 1 1/4" | 0' - 0 9/16" | 0' - 0 11/32" |
| W10X45 | 0.09 SF | 45 | 0' - 8 1/32" | 0' - 10 3/32" | 0' - 1 5/16" | 0' - 0 5/8" | 0' - 0 11/32" |
| W10X39 | 0.08 SF | 39 | 0' - 8" | 0' - 9 29/32" | 0' - 1 3/16" | 0' - 0 17/32" | 0' - 0 5/16" |
| W10X33 | 0.07 SF | 33 | 0' - 7 31/32" | 0' - 9 23/32" | 0' - 1 1/8" | 0' - 0 7/16" | 0' - 0 9/32" |
| W10X30 | 0.06 SF | 30 | 0' - 5 13/16" | 0' - 10 15/32" | 0' - 1 1/8" | 0' - 0 1/2" | 0' - 0 5/16" |
| W10X26 | 0.05 SF | 26 | 0' - 5 25/32" | 0' - 10 11/32" | 0' - 1 1/16" | 0' - 0 7/16" | 0' - 0 1/4" |
| W10X22 | 0.05 SF | 22 | 0' - 5 3/4" | 0' - 10 5/32" | 0' - 0 15/16" | 0' - 0 3/8" | 0' - 0 1/4" |
| W10X19 | 0.04 SF | 19 | 0' - 4 1/32" | 0' - 10 1/4" | 0' - 0 15/16" | 0' - 0 13/32" | 0' - 0 1/4" |
| W10X17 | 0.03 SF | 17 | 0' - 4" | 0' - 10 1/8" | 0' - 0 7/8" | 0' - 0 11/32" | 0' - 0 1/4" |
| W10X15 | 0.03 SF | 15 | 0' - 4" | 0' - 10" | 0' - 0 13/16" | 0' - 0 9/32" | 0' - 0 7/32" |
| W10X12 | 0.02 SF | 12 | 0' - 3 31/32" | 0' - 9 7/8" | 0' - 0 3/4" | 0' - 0 7/32" | 0' - 0 3/16" |
| W8X67 | 0.14 SF | 67 | 0' - 8 9/32" | 0' - 9" | 0' - 1 5/8" | 0' - 0 15/16" | 0' - 0 9/16" |
| W8X58 | 0.12 SF | 58 | 0' - 8 7/32" | 0' - 8 3/4" | 0' - 1 1/2" | 0' - 0 13/16" | 0' - 0 1/2" |
| W8X48 | 0.1 SF | 48 | 0' - 8 1/8" | 0' - 8 1/2" | 0' - 1 3/8" | 0' - 0 11/16" | 0' - 0 13/32" |
| W8X40 | 0.08 SF | 40 | 0' - 8 1/16" | 0' - 8 1/4" | 0' - 1 1/4" | 0' - 0 9/16" | 0' - 0 3/8" |
| W8X35 | 0.07 SF | 35 | 0' - 8 1/32" | 0' - 8 1/8" | 0' - 1 3/16" | 0' - 0 1/2" | 0' - 0 5/16" |
| W8X31 | 0.06 SF | 31 | 0' - 8" | 0' - 8" | 0' - 1 1/8" | 0' - 0 7/16" | 0' - 0 9/32" |
| W8X28 | 0.06 SF | 28 | 0' - 6 17/32" | 0' - 8 1/16" | 0' - 0 15/16" | 0' - 0 15/32" | 0' - 0 9/32" |
| W8X24 | 0.05 SF | 24 | 0' - 6 1/2" | 0' - 7 15/16" | 0' - 0 7/8" | 0' - 0 13/32" | 0' - 0 1/4" |
| W8X21 | 0.04 SF | 21 | 0' - 5 9/32" | 0' - 8 9/32" | 0' - 0 7/8" | 0' - 0 13/32" | 0' - 0 1/4" |
| W8X18 | 0.04 SF | 18 | 0' - 5 1/4" | 0' - 8 1/8" | 0' - 0 13/16" | 0' - 0 11/32" | 0' - 0 7/32" |
| W8X15 | 0.03 SF | 15 | 0' - 4" | 0' - 8 1/8" | 0' - 0 13/16" | 0' - 0 5/16" | 0' - 0 1/4" |
| W8X13 | 0.03 SF | 13 | 0' - 4" | 0' - 8" | 0' - 0 3/4" | 0' - 0 1/4" | 0' - 0 7/32" |
| W8X10 | 0.02 SF | 10 | 0' - 3 15/16" | 0' - 7 7/8" | 0' - 0 11/16" | 0' - 0 7/32" | 0' - 0 5/32" |
| W6X25 | 0.05 SF | 25 | 0' - 6 3/32" | 0' - 6 3/8" | 0' - 0 15/16" | 0' - 0 15/32" | 0' - 0 5/16" |
| W6X20 | 0.04 SF | 20 | 0' - 6 1/32" | 0' - 6 3/16" | 0' - 0 7/8" | 0' - 0 3/8" | 0' - 0 1/4" |
| W6X15 | 0.03 SF | 15 | 0' - 6" | 0' - 6" | 0' - 0 3/4" | 0' - 0 1/4" | 0' - 0 7/32" |
| W6X16 | 0.03 SF | 16 | 0' - 4 1/32" | 0' - 6 9/32" | 0' - 0 7/8" | 0' - 0 13/32" | 0' - 0 1/4" |
| W6X12 | 0.02 SF | 12 | 0' - 4" | 0' - 6 1/32" | 0' - 0 3/4" | 0' - 0 9/32" | 0' - 0 7/32" |
| W6X9 | 0.02 SF | 9 | 0' - 3 15/16" | 0' - 5 29/32" | 0' - 0 11/16" | 0' - 0 7/32" | 0' - 0 5/32" |
| W6X8.5 | 0.02 SF | 8.5 | 0' - 3 15/16" | 0' - 5 27/32" | 0' - 0 11/16" | 0' - 0 3/16" | 0' - 0 5/32" |
| W5X19 | 0.04 SF | 19 | 0' - 5 1/32" | 0' - 5 5/32" | 0' - 0 13/16" | 0' - 0 7/16" | 0' - 0 9/32" |
| W5X16 | 0.03 SF | 16 | 0' - 5" | 0' - 5" | 0' - 0 3/4" | 0' - 0 3/8" | 0' - 0 1/4" |
| W4X13 | 0.03 SF | 13 | 0' - 4 1/16" | 0' - 4 5/32" | 0' - 0 11/16" | 0' - 0 11/32" | 0' - 0 9/32" |

## geometry (parser evidence)
native form markers: Sweep x1
no freeform markers — native parametric forms only
